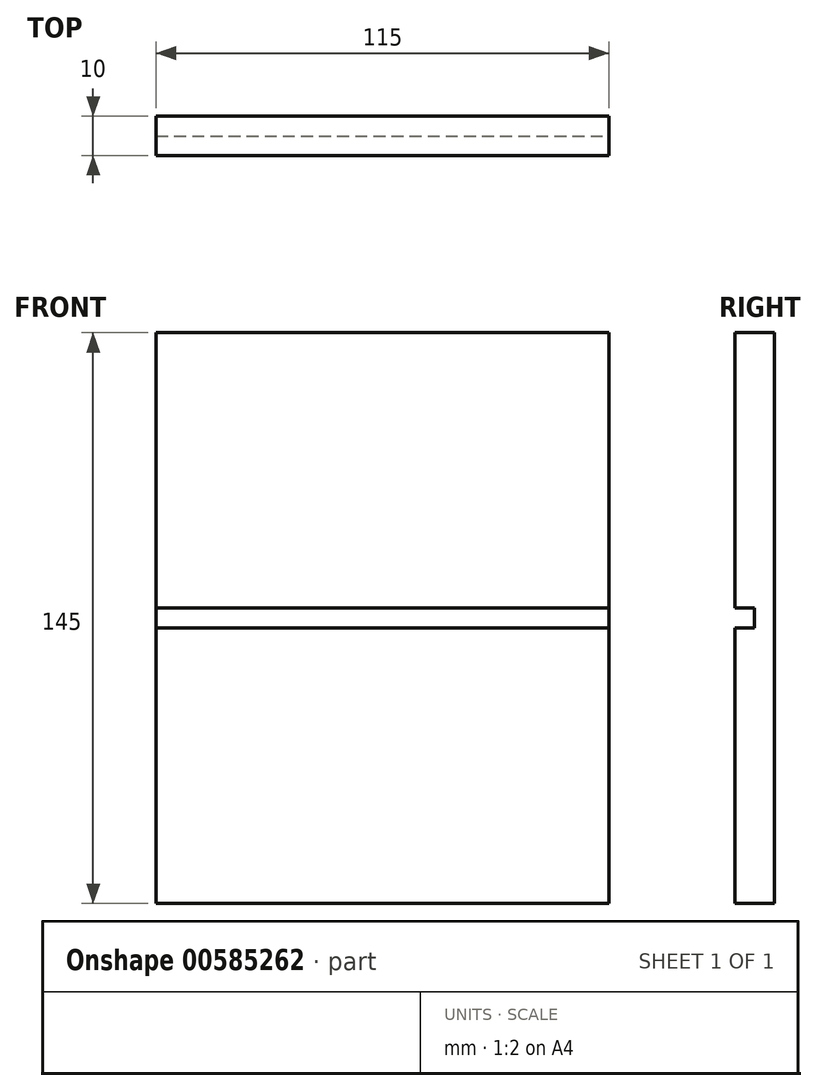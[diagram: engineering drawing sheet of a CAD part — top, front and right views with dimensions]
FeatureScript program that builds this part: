
annotation { "Feature Type Name" : "Feature", "Feature Type Description" : "" }
export const myFeature = defineFeature(function(context is Context, id is Id, definition is map)
    precondition{}
    {
        {
            var Q0;
            Q0=qCreatedBy(makeId("Front.planeOp"),FACE);
            var sketch = newSketch(context, id + "F0", { "sketchPlane" : qUnion([Q0])});
            skLineSegment(sketch, "E0", {"start": v(-48.01, 75.38) * mm, "end": v(66.99, 75.38) * mm});
            skLineSegment(sketch, "E1", {"start": v(66.99, 75.38) * mm, "end": v(66.99, 5.38) * mm});
            skLineSegment(sketch, "E2", {"start": v(66.99, 5.38) * mm, "end": v(66.99, 0.38) * mm});
            skLineSegment(sketch, "E3", {"start": v(66.99, 0.38) * mm, "end": v(66.99, -69.62) * mm});
            skLineSegment(sketch, "E4", {"start": v(66.99, -69.62) * mm, "end": v(-48.01, -69.62) * mm});
            skLineSegment(sketch, "E5", {"start": v(-48.01, -69.62) * mm, "end": v(-48.01, 0.38) * mm});
            skLineSegment(sketch, "E6", {"start": v(-48.01, 0.38) * mm, "end": v(-48.01, 5.38) * mm});
            skLineSegment(sketch, "E7", {"start": v(-48.01, 5.38) * mm, "end": v(-48.01, 75.38) * mm});
            skLineSegment(sketch, "E8", {"start": v(-48.01, 5.38) * mm, "end": v(66.99, 5.38) * mm});
            skLineSegment(sketch, "E9", {"start": v(-48.01, 0.38) * mm, "end": v(66.99, 0.38) * mm});
            skSolve(sketch);
        }
        {
            var Q0;
            Q0=makeQuery(id+"F0.imprint","IMPRINT",FACE,{"disambiguationData":[TD([[makeQuery(id+"F0.imprint","IMPRINT",EDGE,{"derivedFrom":sQuery(id+"F0.wireOp",EDGE,"E2")}),-1.0]])]});
            extrude(context, id + "F1", {"entities" : qUnion([Q0]), "depth" : 5 * mm, "offsetDistance" : 25 * mm});
        }
        {
            var Q0;
            Q0=makeQuery(id+"F0.imprint","IMPRINT",FACE,{"disambiguationData":[TD([[makeQuery(id+"F0.imprint","IMPRINT",EDGE,{"derivedFrom":sQuery(id+"F0.wireOp",EDGE,"E0")}),-1.0]])]});
            var Q1;
            Q1=makeQuery(id+"F0.imprint","IMPRINT",FACE,{"disambiguationData":[TD([[makeQuery(id+"F0.imprint","IMPRINT",EDGE,{"derivedFrom":sQuery(id+"F0.wireOp",EDGE,"E3")}),-1.0]])]});
            extrude(context, id + "F2", {"entities" : qUnion([Q0, Q1]), "operationType" : NewBodyOperationType.ADD, "depth" : 10 * mm, "offsetDistance" : 25 * mm});
        }
    });
